annotation { "Feature Type Name" : "Feature", "Feature Type Description" : "" }
export const myFeature = defineFeature(function(context is Context, id is Id, definition is map)
    precondition{}
    {
        {
            var Q0;
            Q0=qCreatedBy(makeId("Top.planeOp"),FACE);
            var sketch = newSketch(context, id + "F0", { "sketchPlane" : qUnion([Q0])});
            skLineSegment(sketch, "E0.bottom", {"start": v(12.7, 6.6) * mm, "end": v(-12.7, 6.6) * mm});
            skLineSegment(sketch, "E0.top", {"start": v(12.7, -6.6) * mm, "end": v(-12.7, -6.6) * mm});
            skLineSegment(sketch, "E0.left", {"start": v(12.95, 6.35) * mm, "end": v(12.95, -6.35) * mm});
            skLineSegment(sketch, "E0.right", {"start": v(-12.95, 6.35) * mm, "end": v(-12.95, -6.35) * mm});
            skPoint(sketch, "E0.middle", {"position": v(0, 0) * mm});
            skPoint(sketch, "E1.visualSharp", {"position": v(-12.95, 6.6) * mm});
            skArc(sketch, "E1.filletArc", {"start": v(-12.7, 6.6) * mm, "mid": v(-12.88, 6.53) * mm, "end": v(-12.95, 6.35) * mm});
            skPoint(sketch, "E2.visualSharp", {"position": v(12.95, 6.6) * mm});
            skArc(sketch, "E2.filletArc", {"start": v(12.95, 6.35) * mm, "mid": v(12.88, 6.53) * mm, "end": v(12.7, 6.6) * mm});
            skPoint(sketch, "E3.visualSharp", {"position": v(12.95, -6.6) * mm});
            skArc(sketch, "E3.filletArc", {"start": v(12.7, -6.6) * mm, "mid": v(12.88, -6.53) * mm, "end": v(12.95, -6.35) * mm});
            skPoint(sketch, "E4.visualSharp", {"position": v(-12.95, -6.6) * mm});
            skArc(sketch, "E4.filletArc", {"start": v(-12.95, -6.35) * mm, "mid": v(-12.88, -6.53) * mm, "end": v(-12.7, -6.6) * mm});
            skSolve(sketch);
        }
        {
            var Q0;
            Q0 = qSketchRegion(id + "F0", true);
            extrude(context, id + "F1", {"entities" : qUnion([Q0]), "depth" : 0.13 * mm});
        }
        {
            var Q0;
            Q0=makeQuery(id+"F1.opExtrude","CAP_FACE",FACE,{"disambiguationData":[OSD([sQuery(id+"F0.wireOp",EDGE,"E0.bottom"),sQuery(id+"F0.wireOp",EDGE,"E0.top"),sQuery(id+"F0.wireOp",EDGE,"E0.left"),sQuery(id+"F0.wireOp",EDGE,"E0.right"),sQuery(id+"F0.wireOp",EDGE,"E1.filletArc"),sQuery(id+"F0.wireOp",EDGE,"E2.filletArc"),sQuery(id+"F0.wireOp",EDGE,"E3.filletArc"),sQuery(id+"F0.wireOp",EDGE,"E4.filletArc")])],"isStart":false});
            var sketch = newSketch(context, id + "F2", { "sketchPlane" : qUnion([Q0])});
            skSolve(sketch);
        }
        {
            var Q0;
            Q0=makeQuery(id+"F2.imprint","IMPRINT",FACE,{"disambiguationData":[TD([[makeQuery(id+"F2.imprint","IMPRINT",EDGE,{"derivedFrom":makeQuery(id+"F1.opExtrude","CAP_EDGE",EDGE,{"disambiguationData":[OSD([sQuery(id+"F0.wireOp",EDGE,"E0.bottom")])],"isStart":false})}),1.0]])]});
            var sketch = newSketch(context, id + "F3", { "sketchPlane" : qUnion([Q0])});
            skText(sketch, "E5", { "text": "Contains Transmitter Module", "fontName": "OpenSans-Regular.ttf"});
            skText(sketch, "E6", { "text": "FCC ID: Y82-SC14S", "fontName": "OpenSans-Regular.ttf"});
            skText(sketch, "E7", { "text": "IC: 9576A-SC14S", "fontName": "OpenSans-Regular.ttf"});
            skText(sketch, "E8", { "text": "ROO AUDIO", "fontName": "OpenSans-Regular.ttf"});
            skText(sketch, "E9", { "text": "PN:JOE1, SN:", "fontName": "OpenSans-Regular.ttf"});
            const initialGuessF3  = {"E5": [-0.01204, 0.00025, 1, 0, 0.00127], "E6": [-0.00748, -0.00165, 1, 0, 0.00127], "E7": [-0.00667, -0.00356, 1, 0, 0.00127], "E8": [-0.01232, 0.00241, 1, 0, 0.00318], "E9": [-0.01034, -0.00546, 1, 0, 0.00127]};
            skSetInitialGuess(sketch, initialGuessF3);
            skSolve(sketch);
        }
        {
            var Q0;
            Q0 = qSketchRegion(id + "F3", true);
            extrude(context, id + "F4", {"entities" : qUnion([Q0]), "operationType" : NewBodyOperationType.REMOVE, "oppositeDirection" : true, "depth" : 0.03 * mm});
        }
    });